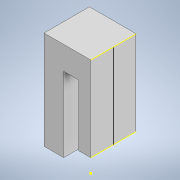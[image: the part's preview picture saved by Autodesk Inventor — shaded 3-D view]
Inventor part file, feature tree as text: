
AUTODESK INVENTOR PART (.ipt)
format: ipt  version: 2020 (Build 240168000, 168)  size: 116,224 bytes
history: native  units: in
note: dims shown in document units (in); Inventor stores cm internally (conversion verified against a paired STEP export)
features: sketch x4, extrude x3
ambient origin geometry x8: Origin, YZ Plane, XZ Plane, XY Plane, X Axis, Y Axis, Z Axis, Center Point
bodies: Solid1 (feature_tree)
feature tree (7):
  extrude  "Extrusion1"  Depth=0.37in
  extrude  "Extrusion2"  Depth=0.19in
  extrude  "Extrusion3"  Depth=0.1in
  sketch  "Sketch5"  dims[d9=0.5in d10=0.0in]
  sketch  "Sketch1"  dims[d0=0.16in d1=0.37in]
  sketch  "Sketch3"  dims[d2=0.8in d3=0.0in d5=0.19in]
  sketch  "Sketch4"  dims[d6=0.22in d7=0.0in d8=0.1in]
